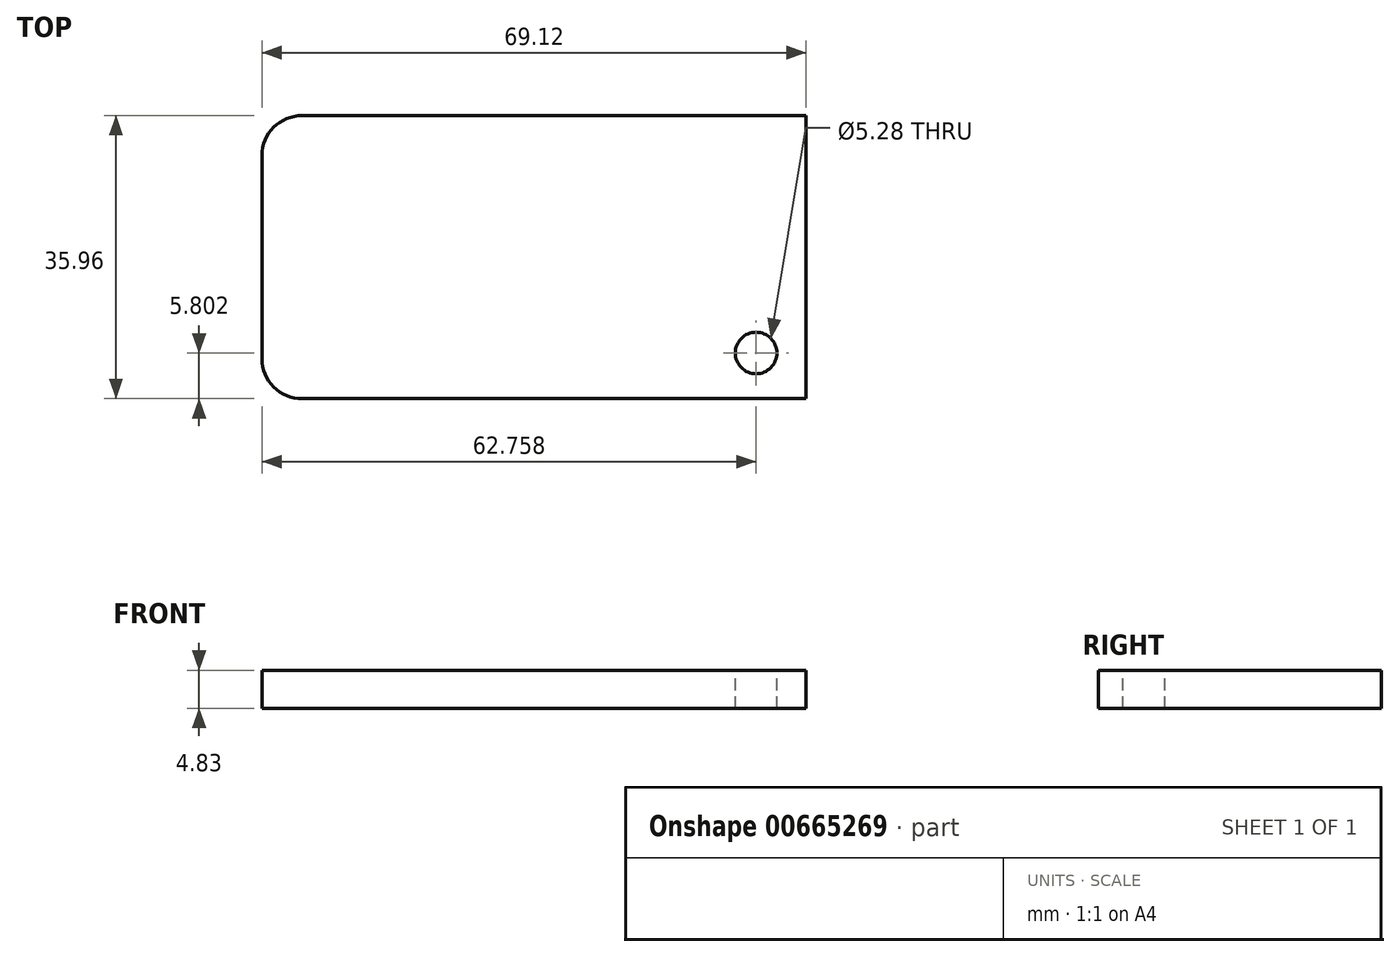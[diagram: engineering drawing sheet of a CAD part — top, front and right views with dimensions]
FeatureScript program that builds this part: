
annotation { "Feature Type Name" : "Feature", "Feature Type Description" : "" }
export const myFeature = defineFeature(function(context is Context, id is Id, definition is map)
    precondition{}
    {
        {
            var Q0;
            Q0=qCreatedBy(makeId("Top.planeOp"),FACE);
            var sketch = newSketch(context, id + "F0", { "sketchPlane" : qUnion([Q0])});
            skLineSegment(sketch, "E0.bottom", {"start": v(0, 0) * mm, "end": v(-69.12, 0) * mm});
            skLineSegment(sketch, "E0.top", {"start": v(0, 35.96) * mm, "end": v(-69.12, 35.96) * mm});
            skLineSegment(sketch, "E0.left", {"start": v(0, 0) * mm, "end": v(0, 35.96) * mm});
            skLineSegment(sketch, "E0.right", {"start": v(-69.12, 0) * mm, "end": v(-69.12, 35.96) * mm});
            skSolve(sketch);
        }
        {
            var Q0;
            Q0=makeQuery(id+"F0.imprint","IMPRINT",FACE,{"disambiguationData":[TD([[makeQuery(id+"F0.imprint","IMPRINT",EDGE,{"derivedFrom":sQuery(id+"F0.wireOp",EDGE,"E0.bottom")}),-1.0]])]});
            extrude(context, id + "F1", {"entities" : qUnion([Q0]), "depth" : 4.83 * mm, "offsetDistance" : 25.4 * mm});
        }
        {
            var Q0;
            Q0=makeQuery(id+"F1.opExtrude","SWEPT_EDGE",EDGE,{"disambiguationData":[OSD([sQuery(id+"F0.wireOp",EDGE,"E0.bottom"),sQuery(id+"F0.wireOp",EDGE,"E0.right")])]});
            fillet(context, id + "F2", {"entities" : qUnion([Q0]), "radius" : 5.08 * mm, "tangentPropagation" : true, "allowEdgeOverflow" : false});
        }
        {
            var Q0;
            Q0=makeQuery(id+"F1.opExtrude","SWEPT_EDGE",EDGE,{"disambiguationData":[OSD([sQuery(id+"F0.wireOp",EDGE,"E0.top"),sQuery(id+"F0.wireOp",EDGE,"E0.right")])]});
            fillet(context, id + "F3", {"entities" : qUnion([Q0]), "radius" : 5.08 * mm, "tangentPropagation" : true, "allowEdgeOverflow" : false});
        }
        {
            var Q0;
            Q0=makeQuery(id+"F1.opExtrude","CAP_FACE",FACE,{"disambiguationData":[OSD([sQuery(id+"F0.wireOp",EDGE,"E0.bottom"),sQuery(id+"F0.wireOp",EDGE,"E0.top"),sQuery(id+"F0.wireOp",EDGE,"E0.left"),sQuery(id+"F0.wireOp",EDGE,"E0.right")])],"isStart":false});
            var sketch = newSketch(context, id + "F4", { "sketchPlane" : qUnion([Q0])});
            skCircle(sketch, "E1", {"center": v(-6.36, 5.8) * mm, "radius": 2.64 * mm});
            skSolve(sketch);
        }
        {
            var Q0;
            Q0=makeQuery(id+"F4.imprint","IMPRINT",FACE,{"disambiguationData":[TD([[makeQuery(id+"F4.imprint","IMPRINT",EDGE,{"derivedFrom":sQuery(id+"F4.wireOp",EDGE,"E1")}),1.0]])]});
            var Q1;
            Q1=sQuery(id+"F4.wireOp",EDGE,"E1");
            extrude(context, id + "F5", {"entities" : qUnion([Q0]), "operationType" : NewBodyOperationType.REMOVE, "surfaceEntities" : qUnion([Q1]), "oppositeDirection" : true, "depth" : 25.4 * mm, "offsetDistance" : 25.4 * mm});
        }
    });
